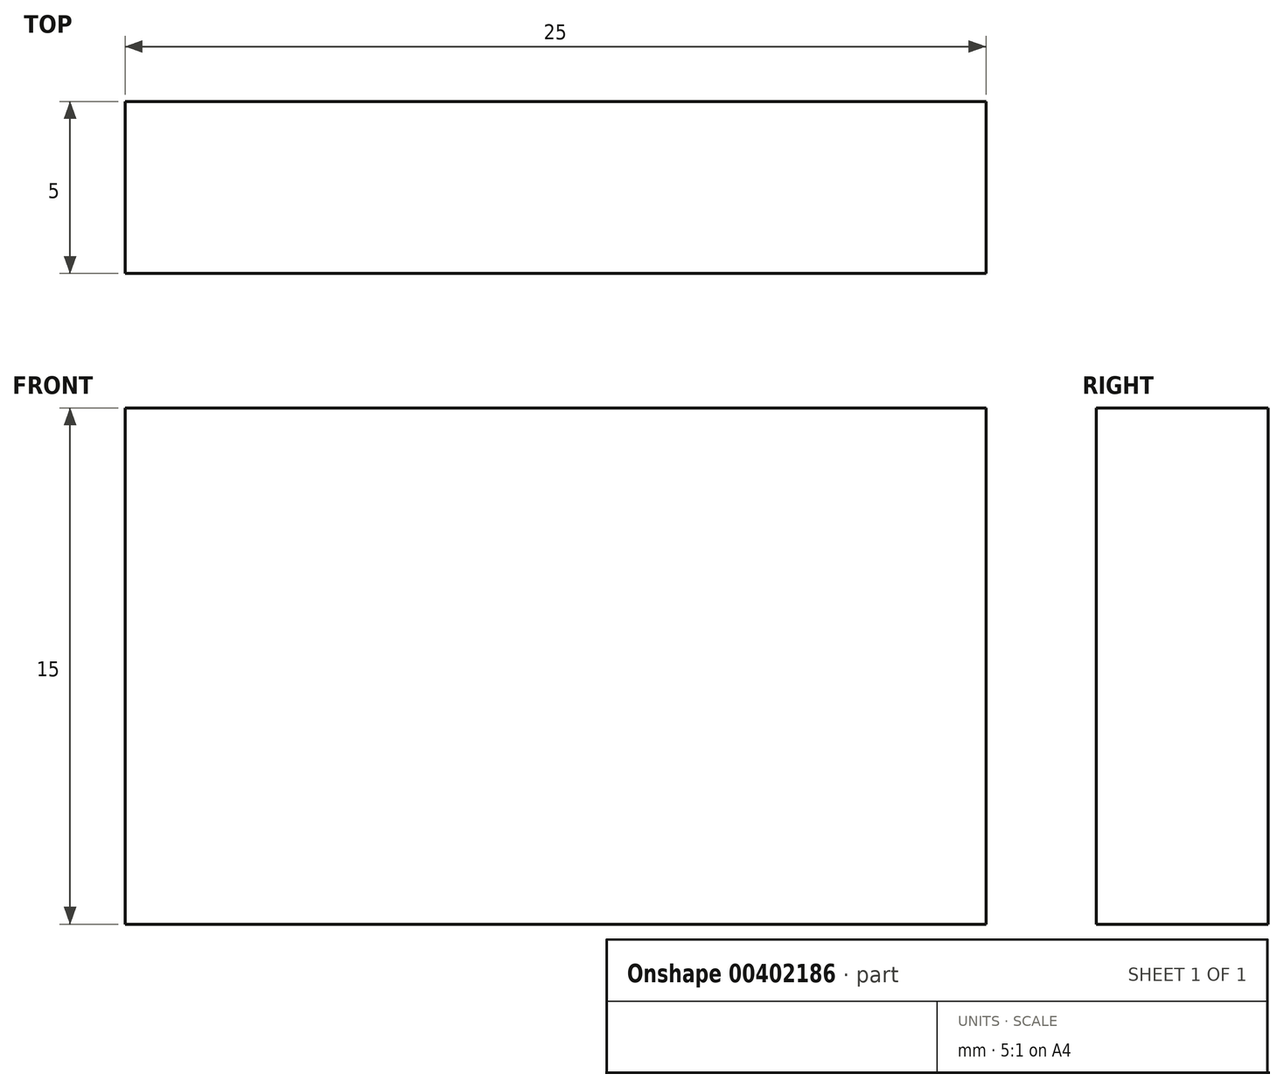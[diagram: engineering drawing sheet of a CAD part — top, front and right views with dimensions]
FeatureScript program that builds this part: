
annotation { "Feature Type Name" : "Feature", "Feature Type Description" : "" }
export const myFeature = defineFeature(function(context is Context, id is Id, definition is map)
    precondition{}
    {
        {
            var Q0;
            Q0=qCreatedBy(makeId("Front.planeOp"),FACE);
            var sketch = newSketch(context, id + "F0", { "sketchPlane" : qUnion([Q0])});
            skLineSegment(sketch, "E0.bottom", {"start": v(12.5, 7.5) * mm, "end": v(-12.5, 7.5) * mm});
            skLineSegment(sketch, "E0.top", {"start": v(12.5, -7.5) * mm, "end": v(-12.5, -7.5) * mm});
            skLineSegment(sketch, "E0.left", {"start": v(12.5, 7.5) * mm, "end": v(12.5, -7.5) * mm});
            skLineSegment(sketch, "E0.right", {"start": v(-12.5, 7.5) * mm, "end": v(-12.5, -7.5) * mm});
            skPoint(sketch, "E0.middle", {"position": v(0, 0) * mm});
            skSolve(sketch);
        }
        {
            var Q0;
            Q0 = qSketchRegion(id + "F0", true);
            extrude(context, id + "F1", {"entities" : qUnion([Q0]), "depth" : 5 * mm});
        }
    });
